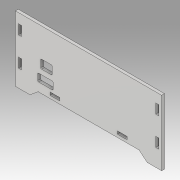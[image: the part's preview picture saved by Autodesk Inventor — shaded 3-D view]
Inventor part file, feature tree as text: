
AUTODESK INVENTOR PART (.ipt)
format: ipt  version: 2019.3 (Build 233278000, 278)  size: 171,520 bytes
history: native  units: mm
features: extrude x2, sketch x2
ambient origin geometry x8: Origin, YZ Plane, XZ Plane, XY Plane, X Axis, Y Axis, Z Axis, Center Point
bodies: Solid1 (feature_tree)
feature tree (4):
  extrude  "Extrusion1"  Depth=10.0mm
  extrude  "Extrusion2"  Depth=10.0mm
  sketch  "Sketch1"  dims[d0=3.0mm d1=10.0mm]
  sketch  "Sketch2"  dims[d2=60.0mm d3=10.0mm d4=152.0mm d5=36.0mm d6=36.0mm d7=3.1mm d8=10.0mm d9=20.0mm d10=5.0mm d11=10.0mm d12=3.0mm d13=3.0mm d14=3.0mm d15=15.0mm d16=15.0mm d17=105.0mm d18=3.0mm d19=0.0mm d20=26.09mm d21=10.0mm d22=0.0mm d23=12.0mm d24=9.0mm d28=20.6mm d29=1.0mm d30=12.75mm d31=37.25mm d32=5.0mm d33=5.0mm d34=16.0mm d35=3.0mm d36=8.0mm d37=1.0mm]
